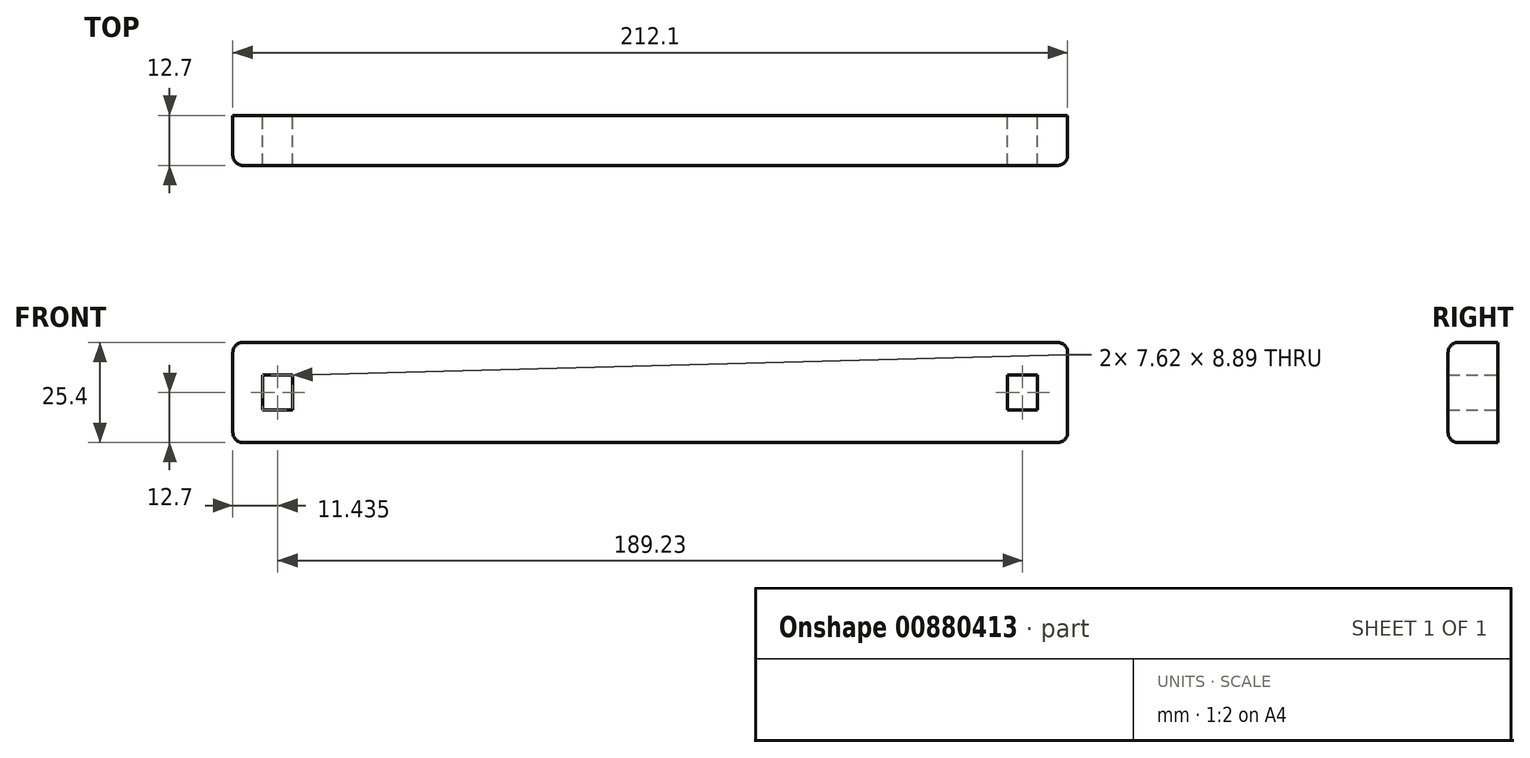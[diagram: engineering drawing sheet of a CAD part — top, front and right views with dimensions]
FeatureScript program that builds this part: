
annotation { "Feature Type Name" : "Feature", "Feature Type Description" : "" }
export const myFeature = defineFeature(function(context is Context, id is Id, definition is map)
    precondition{}
    {
        {
            var Q0;
            Q0=qCreatedBy(makeId("Front.planeOp"),FACE);
            var sketch = newSketch(context, id + "F0", { "sketchPlane" : qUnion([Q0])});
            skLineSegment(sketch, "E0.bottom", {"start": v(106.05, -12.7) * mm, "end": v(-106.05, -12.7) * mm});
            skLineSegment(sketch, "E0.top", {"start": v(106.05, 12.7) * mm, "end": v(-106.05, 12.7) * mm});
            skLineSegment(sketch, "E0.left", {"start": v(106.05, -12.7) * mm, "end": v(106.05, 12.7) * mm});
            skLineSegment(sketch, "E0.right", {"start": v(-106.05, -12.7) * mm, "end": v(-106.05, 12.7) * mm});
            skPoint(sketch, "E0.middle", {"position": v(0, 0) * mm});
            skSolve(sketch);
        }
        {
            var Q0;
            Q0=makeQuery(id+"F0.imprint","IMPRINT",FACE,{"disambiguationData":[TD([[makeQuery(id+"F0.imprint","IMPRINT",EDGE,{"derivedFrom":sQuery(id+"F0.wireOp",EDGE,"E0.bottom")}),-1.0]])]});
            extrude(context, id + "F1", {"entities" : qUnion([Q0]), "depth" : 12.7 * mm, "offsetDistance" : 25.4 * mm});
        }
        {
            var Q0;
            Q0=makeQuery(id+"F1.opExtrude","SWEPT_EDGE",EDGE,{"disambiguationData":[OSD([sQuery(id+"F0.wireOp",EDGE,"E0.top"),sQuery(id+"F0.wireOp",EDGE,"E0.left")])]});
            var Q1;
            Q1=makeQuery(id+"F1.opExtrude","CAP_EDGE",EDGE,{"disambiguationData":[OSD([sQuery(id+"F0.wireOp",EDGE,"E0.left")])],"isStart":false});
            var Q2;
            Q2=makeQuery(id+"F1.opExtrude","CAP_EDGE",EDGE,{"disambiguationData":[OSD([sQuery(id+"F0.wireOp",EDGE,"E0.top")])],"isStart":false});
            var Q3;
            Q3=makeQuery(id+"F1.opExtrude","CAP_EDGE",EDGE,{"disambiguationData":[OSD([sQuery(id+"F0.wireOp",EDGE,"E0.bottom")])],"isStart":false});
            var Q4;
            Q4=makeQuery(id+"F1.opExtrude","CAP_EDGE",EDGE,{"disambiguationData":[OSD([sQuery(id+"F0.wireOp",EDGE,"E0.right")])],"isStart":false});
            var Q5;
            Q5=makeQuery(id+"F1.opExtrude","SWEPT_EDGE",EDGE,{"disambiguationData":[OSD([sQuery(id+"F0.wireOp",EDGE,"E0.top"),sQuery(id+"F0.wireOp",EDGE,"E0.right")])]});
            var Q6;
            Q6=makeQuery(id+"F1.opExtrude","SWEPT_EDGE",EDGE,{"disambiguationData":[OSD([sQuery(id+"F0.wireOp",EDGE,"E0.bottom"),sQuery(id+"F0.wireOp",EDGE,"E0.left")])]});
            var Q7;
            Q7=makeQuery(id+"F1.opExtrude","SWEPT_EDGE",EDGE,{"disambiguationData":[OSD([sQuery(id+"F0.wireOp",EDGE,"E0.bottom"),sQuery(id+"F0.wireOp",EDGE,"E0.right")])]});
            fillet(context, id + "F2", {"entities" : qUnion([Q0, Q1, Q2, Q3, Q4, Q5, Q6, Q7]), "radius" : 2.54 * mm, "tangentPropagation" : true, "allowEdgeOverflow" : false});
        }
        {
            var Q0;
            Q0=makeQuery(id+"F1.opExtrude","CAP_FACE",FACE,{"disambiguationData":[OSD([sQuery(id+"F0.wireOp",EDGE,"E0.bottom"),sQuery(id+"F0.wireOp",EDGE,"E0.top"),sQuery(id+"F0.wireOp",EDGE,"E0.left"),sQuery(id+"F0.wireOp",EDGE,"E0.right")])],"isStart":false});
            var sketch = newSketch(context, id + "F3", { "sketchPlane" : qUnion([Q0])});
            skLineSegment(sketch, "E1", {"start": v(-103.5, 0) * mm, "end": v(-98.42, 0) * mm});
            skLineSegment(sketch, "E2", {"start": v(103.5, 0) * mm, "end": v(98.42, 0) * mm});
            skSolve(sketch);
        }
        {
            var Q0;
            Q0=qCreatedBy(makeId("Front.planeOp"),FACE);
            var sketch = newSketch(context, id + "F4", { "sketchPlane" : qUnion([Q0])});
            skLineSegment(sketch, "E3.bottom", {"start": v(90.8, -4.44) * mm, "end": v(98.42, -4.44) * mm});
            skLineSegment(sketch, "E3.top", {"start": v(90.8, 4.45) * mm, "end": v(98.42, 4.45) * mm});
            skLineSegment(sketch, "E3.left", {"start": v(90.8, -4.44) * mm, "end": v(90.8, 4.45) * mm});
            skLineSegment(sketch, "E3.right", {"start": v(98.42, -4.44) * mm, "end": v(98.42, 4.45) * mm});
            skPoint(sketch, "E3.middle", {"position": v(94.61, 0) * mm});
            skLineSegment(sketch, "E4.bottom", {"start": v(-98.42, -4.45) * mm, "end": v(-90.8, -4.45) * mm});
            skLineSegment(sketch, "E4.top", {"start": v(-98.42, 4.44) * mm, "end": v(-90.8, 4.44) * mm});
            skLineSegment(sketch, "E4.left", {"start": v(-98.42, -4.45) * mm, "end": v(-98.42, 4.44) * mm});
            skLineSegment(sketch, "E4.right", {"start": v(-90.8, -4.45) * mm, "end": v(-90.8, 4.44) * mm});
            skPoint(sketch, "E4.middle", {"position": v(-94.62, 0) * mm});
            skSolve(sketch);
        }
        {
            var Q0;
            Q0 = qSketchRegion(id + "F4", true);
            extrude(context, id + "F5", {"entities" : qUnion([Q0]), "operationType" : NewBodyOperationType.REMOVE, "depth" : 25.4 * mm, "offsetDistance" : 25.4 * mm});
        }
    });
